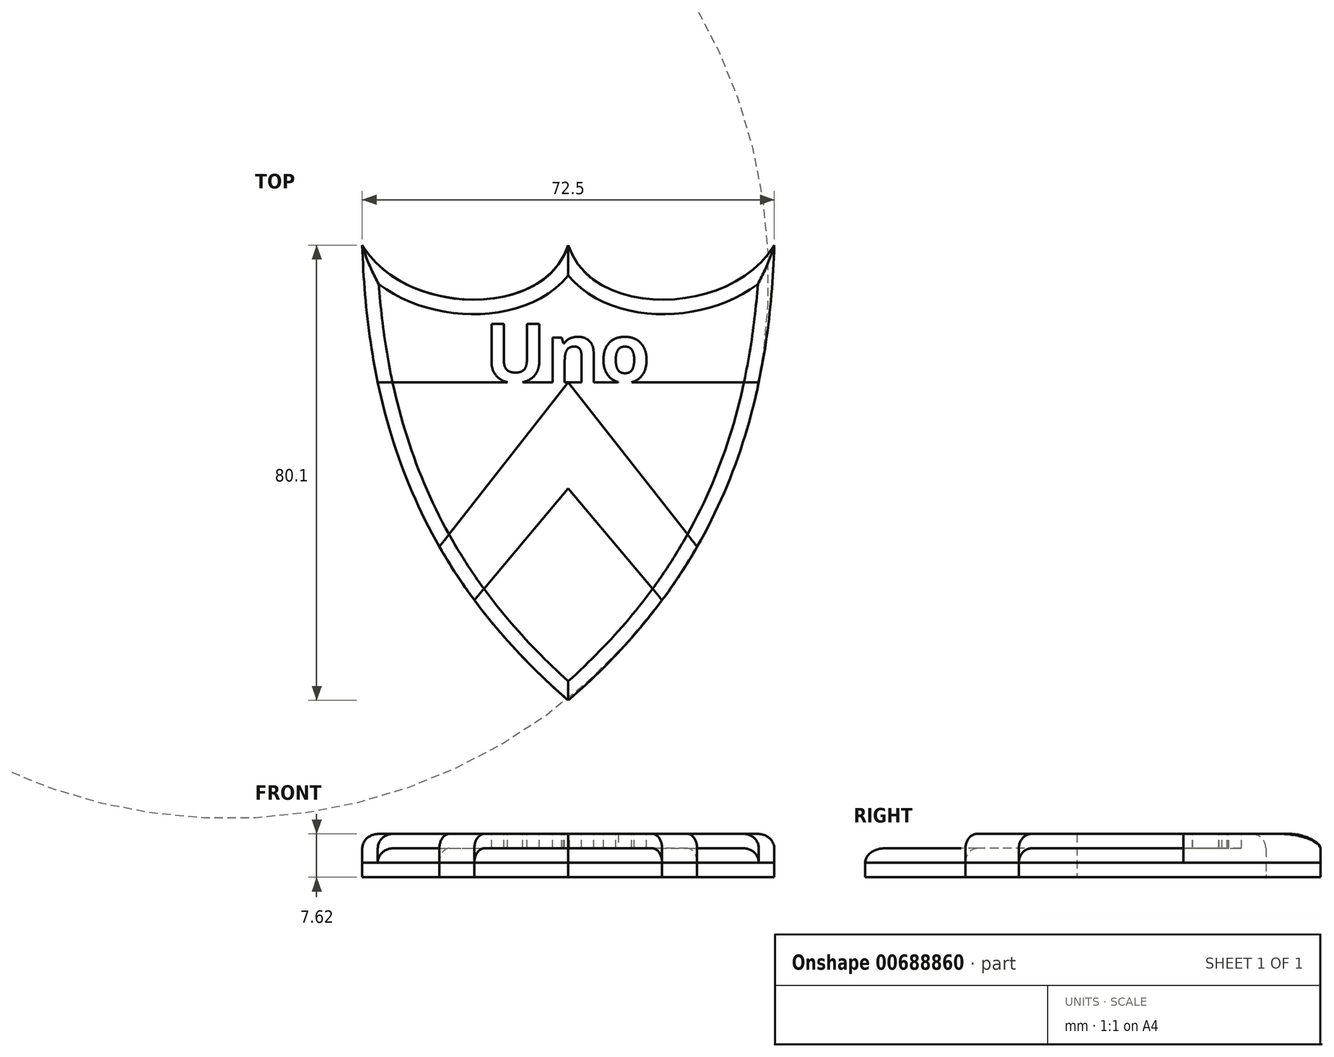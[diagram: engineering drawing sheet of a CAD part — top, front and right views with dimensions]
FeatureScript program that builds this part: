
annotation { "Feature Type Name" : "Feature", "Feature Type Description" : "" }
export const myFeature = defineFeature(function(context is Context, id is Id, definition is map)
    precondition{}
    {
        {
            var Q0;
            Q0=qCreatedBy(makeId("Top.planeOp"),FACE);
            var sketch = newSketch(context, id + "F0", { "sketchPlane" : qUnion([Q0])});
            skFitSpline(sketch, "E0", {"points": [v(-36.25, 24.1) * mm, v(0, -55.99) * mm], "startDerivative": vector(3, -99.72) * mm, "endDerivative": vector(74.22, -64.38) * mm});
            skFitSpline(sketch, "E1", {"points": [v(-36.25, 24.1) * mm, v(0, 24.1) * mm], "startDerivative": vector(22.87, -37.86) * mm, "endDerivative": vector(12.23, 38.86) * mm});
            skFitSpline(sketch, "E2.MirrorCS", {"points": [v(36.25, 24.1) * mm, v(0, -55.99) * mm], "startDerivative": vector(-3, -99.72) * mm, "endDerivative": vector(-74.22, -64.38) * mm});
            skFitSpline(sketch, "E3.MirrorCS", {"points": [v(36.25, 24.1) * mm, v(0, 24.1) * mm], "startDerivative": vector(-22.87, -37.86) * mm, "endDerivative": vector(-12.23, 38.86) * mm});
            skLineSegment(sketch, "E4", {"start": v(-33.52, 0) * mm, "end": v(33.52, 0) * mm});
            skLineSegment(sketch, "E5", {"start": v(-22.68, -28.95) * mm, "end": v(0, 0) * mm});
            skLineSegment(sketch, "E6", {"start": v(0, -18.72) * mm, "end": v(-16.52, -38.35) * mm});
            skLineSegment(sketch, "E7.MirrorCS", {"start": v(0, -18.72) * mm, "end": v(16.52, -38.35) * mm});
            skLineSegment(sketch, "E8.MirrorCS", {"start": v(22.68, -28.95) * mm, "end": v(0, 0) * mm});
            skSolve(sketch);
        }
        {
            var Q0;
            {var subQ1=sQuery(id+"F0.wireOp",EDGE,"E1");Q0=makeQuery(id+"F0.imprint","IMPRINT",FACE,{"disambiguationData":[TD([[makeQuery(id+"F0.imprint","IMPRINT",EDGE,{"derivedFrom":subQ1}),-1.0]])]});}
            extrude(context, id + "F1", {"entities" : qUnion([Q0]), "depth" : 7.62 * mm, "offsetDistance" : 25.4 * mm});
        }
        {
            var Q0;
            {var subQ3=sQuery(id+"F0.wireOp",EDGE,"E5");Q0=makeQuery(id+"F0.imprint","IMPRINT",FACE,{"disambiguationData":[TD([[makeQuery(id+"F0.imprint","IMPRINT",EDGE,{"derivedFrom":subQ3}),1.0]])]});}
            var Q1;
            {var subQ3=sQuery(id+"F0.wireOp",EDGE,"E8.MirrorCS");Q1=makeQuery(id+"F0.imprint","IMPRINT",FACE,{"disambiguationData":[TD([[makeQuery(id+"F0.imprint","IMPRINT",EDGE,{"derivedFrom":subQ3}),-1.0]])]});}
            var Q2;
            {var subQ3=sQuery(id+"F0.wireOp",EDGE,"E6");Q2=makeQuery(id+"F0.imprint","IMPRINT",FACE,{"disambiguationData":[TD([[makeQuery(id+"F0.imprint","IMPRINT",EDGE,{"derivedFrom":subQ3}),1.0]])]});}
            extrude(context, id + "F2", {"entities" : qUnion([Q0, Q1, Q2]), "operationType" : NewBodyOperationType.ADD, "depth" : 5.08 * mm, "offsetDistance" : 25.4 * mm});
        }
        {
            var Q0;
            {var subQ1=sQuery(id+"F0.wireOp",EDGE,"E5");Q0=makeQuery(id+"F0.imprint","IMPRINT",FACE,{"disambiguationData":[TD([[makeQuery(id+"F0.imprint","IMPRINT",EDGE,{"derivedFrom":subQ1}),-1.0]])]});}
            extrude(context, id + "F3", {"entities" : qUnion([Q0]), "depth" : 7.62 * mm, "offsetDistance" : 25.4 * mm});
        }
        {
            var Q0;
            Q0=makeQuery(id+"F1.opExtrude","CAP_FACE",FACE,{"disambiguationData":[OSD([sQuery(id+"F0.wireOp",EDGE,"E0"),sQuery(id+"F0.wireOp",EDGE,"E1"),sQuery(id+"F0.wireOp",EDGE,"E2.MirrorCS"),sQuery(id+"F0.wireOp",EDGE,"E3.MirrorCS"),sQuery(id+"F0.wireOp",EDGE,"E4")])],"isStart":false});
            var sketch = newSketch(context, id + "F4", { "sketchPlane" : qUnion([Q0])});
            skText(sketch, "E9", { "text": "Uno", "fontName": "OpenSans-Bold.ttf"});
            const initialGuessF4  = {"E9": [-0.01473, 0, 1, 0, 0.01033]};
            skSetInitialGuess(sketch, initialGuessF4);
            skSolve(sketch);
        }
        {
            var Q0;
            Q0 = qSketchRegion(id + "F4", true);
            extrude(context, id + "F5", {"entities" : qUnion([Q0]), "operationType" : NewBodyOperationType.REMOVE, "oppositeDirection" : true, "depth" : 2.54 * mm, "offsetDistance" : 25.4 * mm});
        }
        {
            var Q0;
            Q0=makeQuery(id+"F1.opExtrude","CAP_EDGE",EDGE,{"disambiguationData":[OSD([sQuery(id+"F0.wireOp",EDGE,"E0")])],"isStart":false});
            var Q1;
            {var subQ0=sQuery(id+"F0.wireOp",EDGE,"E0");Q1=makeQuery(id+"F2.opExtrude","CAP_EDGE",EDGE,{"disambiguationData":[OSD([subQ0]),TDD([makeQuery(id+"F0.imprint","IMPRINT",EDGE,{"disambiguationData":[TD([[makeQuery(id+"F0.imprint","INTERSECT",VERTEX,{"derivedFrom":[subQ0,sQuery(id+"F0.wireOp",EDGE,"E4")]}),-1.0]])],"derivedFrom":subQ0})])],"isStart":false});}
            var Q2;
            Q2=makeQuery(id+"F1.opExtrude","CAP_EDGE",EDGE,{"disambiguationData":[OSD([sQuery(id+"F0.wireOp",EDGE,"E1")])],"isStart":false});
            var Q3;
            Q3=makeQuery(id+"F1.opExtrude","CAP_EDGE",EDGE,{"disambiguationData":[OSD([sQuery(id+"F0.wireOp",EDGE,"E3.MirrorCS")])],"isStart":false});
            var Q4;
            Q4=makeQuery(id+"F1.opExtrude","CAP_EDGE",EDGE,{"disambiguationData":[OSD([sQuery(id+"F0.wireOp",EDGE,"E2.MirrorCS")])],"isStart":false});
            var Q5;
            {var subQ0=sQuery(id+"F0.wireOp",EDGE,"E2.MirrorCS");Q5=makeQuery(id+"F2.opExtrude","CAP_EDGE",EDGE,{"disambiguationData":[OSD([subQ0]),TDD([makeQuery(id+"F0.imprint","IMPRINT",EDGE,{"disambiguationData":[TD([[makeQuery(id+"F0.imprint","INTERSECT",VERTEX,{"derivedFrom":[subQ0,sQuery(id+"F0.wireOp",EDGE,"E4")]}),-1.0]])],"derivedFrom":subQ0})])],"isStart":false});}
            var Q6;
            {var subQ0=sQuery(id+"F0.wireOp",EDGE,"E0");Q6=makeQuery(id+"F2.opExtrude","CAP_EDGE",EDGE,{"disambiguationData":[OSD([subQ0]),TDD([makeQuery(id+"F0.imprint","IMPRINT",EDGE,{"disambiguationData":[TD([[makeQuery(id+"F0.imprint","INTERSECT",VERTEX,{"derivedFrom":[subQ0,sQuery(id+"F0.wireOp",EDGE,"E2.MirrorCS")]}),1.0]])],"derivedFrom":subQ0})])],"isStart":false});}
            var Q7;
            {var subQ0=sQuery(id+"F0.wireOp",EDGE,"E2.MirrorCS");Q7=makeQuery(id+"F2.opExtrude","CAP_EDGE",EDGE,{"disambiguationData":[OSD([subQ0]),TDD([makeQuery(id+"F0.imprint","IMPRINT",EDGE,{"disambiguationData":[TD([[makeQuery(id+"F0.imprint","INTERSECT",VERTEX,{"derivedFrom":[sQuery(id+"F0.wireOp",EDGE,"E0"),subQ0]}),1.0]])],"derivedFrom":subQ0})])],"isStart":false});}
            fillet(context, id + "F6", {"entities" : qUnion([Q0, Q1, Q2, Q3, Q4, Q5, Q6, Q7]), "radius" : 2.54 * mm, "tangentPropagation" : true, "allowEdgeOverflow" : false});
        }
        {
            var Q0;
            Q0=makeQuery(id+"F3.opExtrude","CAP_EDGE",EDGE,{"disambiguationData":[OSD([sQuery(id+"F0.wireOp",EDGE,"E0")])],"isStart":false});
            var Q1;
            Q1=makeQuery(id+"F3.opExtrude","CAP_EDGE",EDGE,{"disambiguationData":[OSD([sQuery(id+"F0.wireOp",EDGE,"E2.MirrorCS")])],"isStart":false});
            fillet(context, id + "F7", {"entities" : qUnion([Q0, Q1]), "radius" : 2.54 * mm, "tangentPropagation" : true, "allowEdgeOverflow" : false});
        }
        {
            var Q0;
            Q0 = qSketchRegion(id + "F0", true);
            extrude(context, id + "F8", {"entities" : qUnion([Q0]), "depth" : 2.54 * mm, "offsetDistance" : 25.4 * mm});
        }
    });
